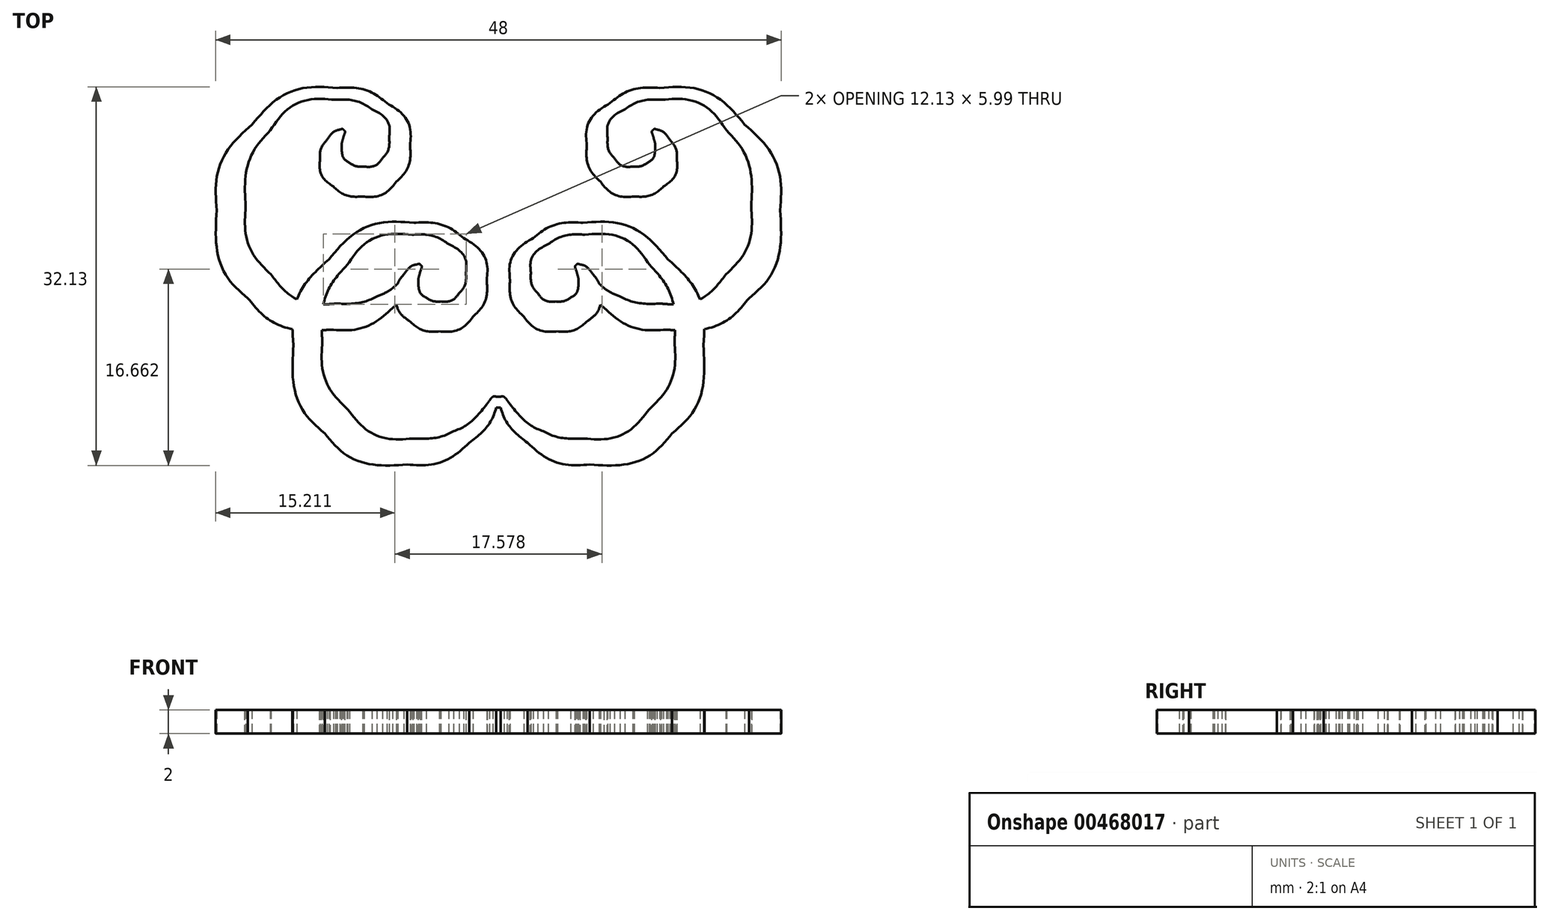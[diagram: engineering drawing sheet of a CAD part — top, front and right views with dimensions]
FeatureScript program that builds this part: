
annotation { "Feature Type Name" : "Feature", "Feature Type Description" : "" }
export const myFeature = defineFeature(function(context is Context, id is Id, definition is map)
    precondition{}
    {
        {
            var Q0;
            Q0=qCreatedBy(makeId("Top.planeOp"),FACE);
            var sketch = newSketch(context, id + "F0", { "sketchPlane" : qUnion([Q0])});
            skFitSpline(sketch, "E0", {"points": [v(-6.53, 0.98) * mm, v(-6.53, 0.79) * mm, v(-6.59, 0.56) * mm, v(-6.7, 0.3) * mm]});
            skFitSpline(sketch, "E1", {"points": [v(-6.7, 0.3) * mm, v(-7.12, -0.8) * mm, v(-7.89, -1.79) * mm, v(-8.99, -2.69) * mm]});
            skFitSpline(sketch, "E2", {"points": [v(-8.99, -2.69) * mm, v(-10.5, -3.92) * mm, v(-12.26, -4.54) * mm, v(-14.26, -4.54) * mm]});
            skFitSpline(sketch, "E3", {"points": [v(-14.26, -4.54) * mm, v(-17.2, -4.54) * mm, v(-19.53, -3.65) * mm, v(-21.26, -1.88) * mm]});
            skFitSpline(sketch, "E4", {"points": [v(-21.26, -1.88) * mm, v(-23.03, -0.07) * mm, v(-23.91, 2.42) * mm, v(-23.91, 5.6) * mm]});
            skFitSpline(sketch, "E5", {"points": [v(-23.91, 5.6) * mm, v(-23.91, 8.38) * mm, v(-22.91, 10.8) * mm, v(-20.9, 12.87) * mm]});
            skFitSpline(sketch, "E6", {"points": [v(-20.9, 12.87) * mm, v(-18.9, 14.94) * mm, v(-16.5, 15.98) * mm, v(-13.7, 15.98) * mm]});
            skFitSpline(sketch, "E7", {"points": [v(-13.7, 15.98) * mm, v(-12.09, 15.98) * mm, v(-10.68, 15.55) * mm, v(-9.47, 14.7) * mm]});
            skFitSpline(sketch, "E8", {"points": [v(-9.47, 14.7) * mm, v(-8.16, 13.75) * mm, v(-7.5, 12.56) * mm, v(-7.5, 11.11) * mm]});
            skFitSpline(sketch, "E9", {"points": [v(-7.5, 11.11) * mm, v(-7.5, 9.9) * mm, v(-7.89, 8.86) * mm, v(-8.66, 8.03) * mm]});
            skFitSpline(sketch, "E10", {"points": [v(-8.66, 8.03) * mm, v(-9.43, 7.19) * mm, v(-10.38, 6.77) * mm, v(-11.52, 6.77) * mm]});
            skFitSpline(sketch, "E11", {"points": [v(-11.52, 6.77) * mm, v(-12.49, 6.77) * mm, v(-13.32, 7.05) * mm, v(-14.02, 7.61) * mm]});
            skFitSpline(sketch, "E12", {"points": [v(-14.02, 7.61) * mm, v(-14.77, 8.22) * mm, v(-15.14, 8.98) * mm, v(-15.14, 9.9) * mm]});
            skFitSpline(sketch, "E13", {"points": [v(-15.14, 9.9) * mm, v(-15.14, 10.5) * mm, v(-14.94, 11.07) * mm, v(-14.54, 11.6) * mm]});
            skFitSpline(sketch, "E14", {"points": [v(-14.54, 11.6) * mm, v(-14.2, 12.06) * mm, v(-13.83, 12.35) * mm, v(-13.45, 12.44) * mm]});
            skFitSpline(sketch, "E15", {"points": [v(-13.45, 12.44) * mm, v(-13.3, 12.5) * mm, v(-13.2, 12.48) * mm, v(-13.11, 12.4) * mm]});
            skFitSpline(sketch, "E16", {"points": [v(-13.11, 12.4) * mm, v(-13.03, 12.32) * mm, v(-13.01, 12.23) * mm, v(-13.05, 12.12) * mm]});
            skFitSpline(sketch, "E17", {"points": [v(-13.05, 12.12) * mm, v(-13.12, 11.93) * mm, v(-13.17, 11.78) * mm, v(-13.2, 11.66) * mm]});
            skFitSpline(sketch, "E18", {"points": [v(-13.2, 11.66) * mm, v(-13.27, 11.39) * mm, v(-13.31, 11.15) * mm, v(-13.31, 10.93) * mm]});
            skFitSpline(sketch, "E19", {"points": [v(-13.31, 10.93) * mm, v(-13.31, 10.78) * mm, v(-13.3, 10.67) * mm, v(-13.3, 10.59) * mm]});
            skFitSpline(sketch, "E20", {"points": [v(-13.3, 10.59) * mm, v(-13.21, 10.17) * mm, v(-13, 9.86) * mm, v(-12.64, 9.63) * mm]});
            skFitSpline(sketch, "E21", {"points": [v(-12.64, 9.63) * mm, v(-12.28, 9.41) * mm, v(-11.87, 9.3) * mm, v(-11.4, 9.3) * mm]});
            skFitSpline(sketch, "E22", {"points": [v(-11.4, 9.3) * mm, v(-10.76, 9.3) * mm, v(-10.24, 9.54) * mm, v(-9.85, 10) * mm]});
            skFitSpline(sketch, "E23", {"points": [v(-9.85, 10) * mm, v(-9.46, 10.48) * mm, v(-9.27, 11.06) * mm, v(-9.27, 11.76) * mm]});
            skFitSpline(sketch, "E24", {"points": [v(-9.27, 11.76) * mm, v(-9.27, 12.78) * mm, v(-9.76, 13.58) * mm, v(-10.74, 14.17) * mm]});
            skFitSpline(sketch, "E25", {"points": [v(-10.74, 14.17) * mm, v(-11.62, 14.7) * mm, v(-12.66, 14.97) * mm, v(-13.86, 14.97) * mm]});
            skFitSpline(sketch, "E26", {"points": [v(-13.86, 14.97) * mm, v(-16.12, 14.97) * mm, v(-17.96, 14.11) * mm, v(-19.36, 12.39) * mm]});
            skFitSpline(sketch, "E27", {"points": [v(-19.36, 12.39) * mm, v(-20.76, 10.67) * mm, v(-21.46, 8.51) * mm, v(-21.46, 5.92) * mm]});
            skFitSpline(sketch, "E28", {"points": [v(-21.46, 5.92) * mm, v(-21.46, 3.67) * mm, v(-20.74, 1.75) * mm, v(-19.3, 0.15) * mm]});
            skFitSpline(sketch, "E29", {"points": [v(-19.3, 0.15) * mm, v(-17.82, -1.5) * mm, v(-15.97, -2.32) * mm, v(-13.78, -2.32) * mm]});
            skFitSpline(sketch, "E30", {"points": [v(-13.78, -2.32) * mm, v(-12.4, -2.32) * mm, v(-11.24, -2.12) * mm, v(-10.33, -1.7) * mm]});
            skFitSpline(sketch, "E31", {"points": [v(-10.33, -1.7) * mm, v(-9.4, -1.3) * mm, v(-8.47, -0.54) * mm, v(-7.5, 0.57) * mm]});
            skFitSpline(sketch, "E32", {"points": [v(-7.5, 0.57) * mm, v(-7.49, 0.6) * mm, v(-7.4, 0.71) * mm, v(-7.26, 0.92) * mm]});
            skFitSpline(sketch, "E33", {"points": [v(-7.26, 0.92) * mm, v(-7.15, 1.06) * mm, v(-7.06, 1.16) * mm, v(-6.98, 1.22) * mm]});
            skFitSpline(sketch, "E34", {"points": [v(-6.98, 1.22) * mm, v(-6.91, 1.26) * mm, v(-6.82, 1.26) * mm, v(-6.7, 1.23) * mm]});
            skFitSpline(sketch, "E35", {"points": [v(-6.7, 1.23) * mm, v(-6.6, 1.2) * mm, v(-6.53, 1.1) * mm, v(-6.53, 0.98) * mm]});
            skFitSpline(sketch, "E36", {"points": [v(-0.02, -10.47) * mm, v(-0.02, -10.66) * mm, v(-0.08, -10.89) * mm, v(-0.18, -11.15) * mm]});
            skFitSpline(sketch, "E37", {"points": [v(-0.18, -11.15) * mm, v(-0.61, -12.24) * mm, v(-1.38, -13.23) * mm, v(-2.48, -14.13) * mm]});
            skFitSpline(sketch, "E38", {"points": [v(-2.48, -14.13) * mm, v(-4, -15.36) * mm, v(-5.75, -15.98) * mm, v(-7.75, -15.98) * mm]});
            skFitSpline(sketch, "E39", {"points": [v(-7.75, -15.98) * mm, v(-10.68, -15.98) * mm, v(-13.02, -15.1) * mm, v(-14.75, -13.33) * mm]});
            skFitSpline(sketch, "E40", {"points": [v(-14.75, -13.33) * mm, v(-16.52, -11.52) * mm, v(-17.4, -9.02) * mm, v(-17.4, -5.84) * mm]});
            skFitSpline(sketch, "E41", {"points": [v(-17.4, -5.84) * mm, v(-17.4, -3.07) * mm, v(-16.4, -0.64) * mm, v(-14.4, 1.43) * mm]});
            skFitSpline(sketch, "E42", {"points": [v(-14.4, 1.43) * mm, v(-12.39, 3.5) * mm, v(-9.99, 4.54) * mm, v(-7.18, 4.54) * mm]});
            skFitSpline(sketch, "E43", {"points": [v(-7.18, 4.54) * mm, v(-5.57, 4.54) * mm, v(-4.17, 4.1) * mm, v(-2.96, 3.25) * mm]});
            skFitSpline(sketch, "E44", {"points": [v(-2.96, 3.25) * mm, v(-1.64, 2.3) * mm, v(-0.99, 1.12) * mm, v(-0.99, -0.33) * mm]});
            skFitSpline(sketch, "E45", {"points": [v(-0.99, -0.33) * mm, v(-0.99, -1.55) * mm, v(-1.37, -2.58) * mm, v(-2.14, -3.42) * mm]});
            skFitSpline(sketch, "E46", {"points": [v(-2.14, -3.42) * mm, v(-2.92, -4.26) * mm, v(-3.87, -4.68) * mm, v(-5.01, -4.68) * mm]});
            skFitSpline(sketch, "E47", {"points": [v(-5.01, -4.68) * mm, v(-5.98, -4.68) * mm, v(-6.8, -4.4) * mm, v(-7.5, -3.83) * mm]});
            skFitSpline(sketch, "E48", {"points": [v(-7.5, -3.83) * mm, v(-8.26, -3.23) * mm, v(-8.63, -2.46) * mm, v(-8.63, -1.54) * mm]});
            skFitSpline(sketch, "E49", {"points": [v(-8.63, -1.54) * mm, v(-8.63, -0.94) * mm, v(-8.43, -0.37) * mm, v(-8.03, 0.15) * mm]});
            skFitSpline(sketch, "E50", {"points": [v(-8.03, 0.15) * mm, v(-7.68, 0.62) * mm, v(-7.32, 0.9) * mm, v(-6.94, 1) * mm]});
            skFitSpline(sketch, "E51", {"points": [v(-6.94, 1) * mm, v(-6.8, 1.05) * mm, v(-6.68, 1.04) * mm, v(-6.6, 0.95) * mm]});
            skFitSpline(sketch, "E52", {"points": [v(-6.6, 0.95) * mm, v(-6.52, 0.87) * mm, v(-6.5, 0.78) * mm, v(-6.54, 0.67) * mm]});
            skFitSpline(sketch, "E53", {"points": [v(-6.54, 0.67) * mm, v(-6.6, 0.49) * mm, v(-6.65, 0.33) * mm, v(-6.68, 0.21) * mm]});
            skFitSpline(sketch, "E54", {"points": [v(-6.68, 0.21) * mm, v(-6.76, -0.06) * mm, v(-6.8, -0.3) * mm, v(-6.8, -0.51) * mm]});
            skFitSpline(sketch, "E55", {"points": [v(-6.8, -0.51) * mm, v(-6.8, -0.66) * mm, v(-6.8, -0.77) * mm, v(-6.78, -0.86) * mm]});
            skFitSpline(sketch, "E56", {"points": [v(-6.78, -0.86) * mm, v(-6.7, -1.27) * mm, v(-6.48, -1.59) * mm, v(-6.13, -1.81) * mm]});
            skFitSpline(sketch, "E57", {"points": [v(-6.13, -1.81) * mm, v(-5.77, -2.03) * mm, v(-5.36, -2.14) * mm, v(-4.89, -2.14) * mm]});
            skFitSpline(sketch, "E58", {"points": [v(-4.89, -2.14) * mm, v(-4.25, -2.14) * mm, v(-3.73, -1.9) * mm, v(-3.34, -1.44) * mm]});
            skFitSpline(sketch, "E59", {"points": [v(-3.34, -1.44) * mm, v(-2.95, -0.97) * mm, v(-2.76, -0.39) * mm, v(-2.76, 0.31) * mm]});
            skFitSpline(sketch, "E60", {"points": [v(-2.76, 0.31) * mm, v(-2.76, 1.33) * mm, v(-3.25, 2.13) * mm, v(-4.23, 2.72) * mm]});
            skFitSpline(sketch, "E61", {"points": [v(-4.23, 2.72) * mm, v(-5.11, 3.26) * mm, v(-6.15, 3.53) * mm, v(-7.34, 3.53) * mm]});
            skFitSpline(sketch, "E62", {"points": [v(-7.34, 3.53) * mm, v(-9.6, 3.53) * mm, v(-11.44, 2.67) * mm, v(-12.84, 0.94) * mm]});
            skFitSpline(sketch, "E63", {"points": [v(-12.84, 0.94) * mm, v(-14.25, -0.78) * mm, v(-14.95, -2.93) * mm, v(-14.95, -5.52) * mm]});
            skFitSpline(sketch, "E64", {"points": [v(-14.95, -5.52) * mm, v(-14.95, -7.77) * mm, v(-14.23, -9.7) * mm, v(-12.8, -11.3) * mm]});
            skFitSpline(sketch, "E65", {"points": [v(-12.8, -11.3) * mm, v(-11.3, -12.94) * mm, v(-9.46, -13.77) * mm, v(-7.26, -13.77) * mm]});
            skFitSpline(sketch, "E66", {"points": [v(-7.26, -13.77) * mm, v(-5.88, -13.77) * mm, v(-4.73, -13.56) * mm, v(-3.81, -13.15) * mm]});
            skFitSpline(sketch, "E67", {"points": [v(-3.81, -13.15) * mm, v(-2.9, -12.75) * mm, v(-1.95, -11.98) * mm, v(-0.99, -10.87) * mm]});
            skFitSpline(sketch, "E68", {"points": [v(-0.99, -10.87) * mm, v(-0.97, -10.85) * mm, v(-0.9, -10.73) * mm, v(-0.75, -10.53) * mm]});
            skFitSpline(sketch, "E69", {"points": [v(-0.75, -10.53) * mm, v(-0.64, -10.38) * mm, v(-0.55, -10.28) * mm, v(-0.46, -10.23) * mm]});
            skFitSpline(sketch, "E70", {"points": [v(-0.46, -10.23) * mm, v(-0.4, -10.19) * mm, v(-0.3, -10.18) * mm, v(-0.2, -10.22) * mm]});
            skFitSpline(sketch, "E71", {"points": [v(-0.2, -10.22) * mm, v(-0.08, -10.25) * mm, v(-0.02, -10.34) * mm, v(-0.02, -10.47) * mm]});
            skFitSpline(sketch, "E72", {"points": [v(6.7, 1.23) * mm, v(6.82, 1.26) * mm, v(6.91, 1.26) * mm, v(6.98, 1.22) * mm]});
            skFitSpline(sketch, "E73", {"points": [v(6.98, 1.22) * mm, v(7.06, 1.16) * mm, v(7.15, 1.06) * mm, v(7.26, 0.92) * mm]});
            skFitSpline(sketch, "E74", {"points": [v(7.26, 0.92) * mm, v(7.4, 0.71) * mm, v(7.49, 0.6) * mm, v(7.5, 0.57) * mm]});
            skFitSpline(sketch, "E75", {"points": [v(7.5, 0.57) * mm, v(8.47, -0.54) * mm, v(9.4, -1.3) * mm, v(10.33, -1.7) * mm]});
            skFitSpline(sketch, "E76", {"points": [v(10.33, -1.7) * mm, v(11.24, -2.12) * mm, v(12.4, -2.32) * mm, v(13.78, -2.32) * mm]});
            skFitSpline(sketch, "E77", {"points": [v(13.78, -2.32) * mm, v(15.97, -2.32) * mm, v(17.82, -1.5) * mm, v(19.3, 0.15) * mm]});
            skFitSpline(sketch, "E78", {"points": [v(19.3, 0.15) * mm, v(20.74, 1.75) * mm, v(21.46, 3.67) * mm, v(21.46, 5.92) * mm]});
            skFitSpline(sketch, "E79", {"points": [v(21.46, 5.92) * mm, v(21.46, 8.51) * mm, v(20.76, 10.67) * mm, v(19.36, 12.39) * mm]});
            skFitSpline(sketch, "E80", {"points": [v(19.36, 12.39) * mm, v(17.96, 14.11) * mm, v(16.12, 14.97) * mm, v(13.86, 14.97) * mm]});
            skFitSpline(sketch, "E81", {"points": [v(13.86, 14.97) * mm, v(12.66, 14.97) * mm, v(11.62, 14.7) * mm, v(10.74, 14.17) * mm]});
            skFitSpline(sketch, "E82", {"points": [v(10.74, 14.17) * mm, v(9.76, 13.58) * mm, v(9.27, 12.78) * mm, v(9.27, 11.76) * mm]});
            skFitSpline(sketch, "E83", {"points": [v(9.27, 11.76) * mm, v(9.27, 11.06) * mm, v(9.46, 10.48) * mm, v(9.85, 10) * mm]});
            skFitSpline(sketch, "E84", {"points": [v(9.85, 10) * mm, v(10.24, 9.54) * mm, v(10.76, 9.3) * mm, v(11.4, 9.3) * mm]});
            skFitSpline(sketch, "E85", {"points": [v(11.4, 9.3) * mm, v(11.87, 9.3) * mm, v(12.28, 9.41) * mm, v(12.64, 9.63) * mm]});
            skFitSpline(sketch, "E86", {"points": [v(12.64, 9.63) * mm, v(13, 9.86) * mm, v(13.21, 10.17) * mm, v(13.3, 10.59) * mm]});
            skFitSpline(sketch, "E87", {"points": [v(13.3, 10.59) * mm, v(13.3, 10.67) * mm, v(13.31, 10.78) * mm, v(13.31, 10.93) * mm]});
            skFitSpline(sketch, "E88", {"points": [v(13.31, 10.93) * mm, v(13.31, 11.15) * mm, v(13.27, 11.39) * mm, v(13.2, 11.66) * mm]});
            skFitSpline(sketch, "E89", {"points": [v(13.2, 11.66) * mm, v(13.17, 11.78) * mm, v(13.12, 11.93) * mm, v(13.05, 12.12) * mm]});
            skFitSpline(sketch, "E90", {"points": [v(13.05, 12.12) * mm, v(13.01, 12.23) * mm, v(13.03, 12.32) * mm, v(13.11, 12.4) * mm]});
            skFitSpline(sketch, "E91", {"points": [v(13.11, 12.4) * mm, v(13.2, 12.48) * mm, v(13.3, 12.5) * mm, v(13.45, 12.44) * mm]});
            skFitSpline(sketch, "E92", {"points": [v(13.45, 12.44) * mm, v(13.83, 12.35) * mm, v(14.2, 12.06) * mm, v(14.54, 11.6) * mm]});
            skFitSpline(sketch, "E93", {"points": [v(14.54, 11.6) * mm, v(14.94, 11.07) * mm, v(15.14, 10.5) * mm, v(15.14, 9.9) * mm]});
            skFitSpline(sketch, "E94", {"points": [v(15.14, 9.9) * mm, v(15.14, 8.98) * mm, v(14.77, 8.22) * mm, v(14.02, 7.61) * mm]});
            skFitSpline(sketch, "E95", {"points": [v(14.02, 7.61) * mm, v(13.32, 7.05) * mm, v(12.49, 6.77) * mm, v(11.52, 6.77) * mm]});
            skFitSpline(sketch, "E96", {"points": [v(11.52, 6.77) * mm, v(10.38, 6.77) * mm, v(9.43, 7.19) * mm, v(8.66, 8.03) * mm]});
            skFitSpline(sketch, "E97", {"points": [v(8.66, 8.03) * mm, v(7.89, 8.86) * mm, v(7.5, 9.9) * mm, v(7.5, 11.11) * mm]});
            skFitSpline(sketch, "E98", {"points": [v(7.5, 11.11) * mm, v(7.5, 12.56) * mm, v(8.16, 13.75) * mm, v(9.47, 14.7) * mm]});
            skFitSpline(sketch, "E99", {"points": [v(9.47, 14.7) * mm, v(10.68, 15.55) * mm, v(12.09, 15.98) * mm, v(13.7, 15.98) * mm]});
            skFitSpline(sketch, "E100", {"points": [v(13.7, 15.98) * mm, v(16.5, 15.98) * mm, v(18.9, 14.94) * mm, v(20.9, 12.87) * mm]});
            skFitSpline(sketch, "E101", {"points": [v(20.9, 12.87) * mm, v(22.91, 10.8) * mm, v(23.91, 8.38) * mm, v(23.91, 5.6) * mm]});
            skFitSpline(sketch, "E102", {"points": [v(23.91, 5.6) * mm, v(23.91, 2.42) * mm, v(23.03, -0.07) * mm, v(21.26, -1.88) * mm]});
            skFitSpline(sketch, "E103", {"points": [v(21.26, -1.88) * mm, v(19.53, -3.65) * mm, v(17.2, -4.54) * mm, v(14.26, -4.54) * mm]});
            skFitSpline(sketch, "E104", {"points": [v(14.26, -4.54) * mm, v(12.26, -4.54) * mm, v(10.5, -3.92) * mm, v(8.99, -2.68) * mm]});
            skFitSpline(sketch, "E105", {"points": [v(8.99, -2.68) * mm, v(7.89, -1.79) * mm, v(7.12, -0.8) * mm, v(6.7, 0.3) * mm]});
            skFitSpline(sketch, "E106", {"points": [v(6.7, 0.3) * mm, v(6.59, 0.56) * mm, v(6.53, 0.79) * mm, v(6.53, 0.98) * mm]});
            skFitSpline(sketch, "E107", {"points": [v(6.53, 0.98) * mm, v(6.53, 1.1) * mm, v(6.6, 1.2) * mm, v(6.7, 1.23) * mm]});
            skFitSpline(sketch, "E108", {"points": [v(0.2, -10.22) * mm, v(0.3, -10.18) * mm, v(0.4, -10.19) * mm, v(0.46, -10.23) * mm]});
            skFitSpline(sketch, "E109", {"points": [v(0.46, -10.23) * mm, v(0.55, -10.28) * mm, v(0.64, -10.38) * mm, v(0.75, -10.53) * mm]});
            skFitSpline(sketch, "E110", {"points": [v(0.75, -10.53) * mm, v(0.9, -10.73) * mm, v(0.97, -10.85) * mm, v(0.99, -10.87) * mm]});
            skFitSpline(sketch, "E111", {"points": [v(0.99, -10.87) * mm, v(1.95, -11.98) * mm, v(2.9, -12.75) * mm, v(3.81, -13.15) * mm]});
            skFitSpline(sketch, "E112", {"points": [v(3.81, -13.15) * mm, v(4.73, -13.56) * mm, v(5.88, -13.77) * mm, v(7.26, -13.77) * mm]});
            skFitSpline(sketch, "E113", {"points": [v(7.26, -13.77) * mm, v(9.46, -13.77) * mm, v(11.3, -12.94) * mm, v(12.8, -11.3) * mm]});
            skFitSpline(sketch, "E114", {"points": [v(12.8, -11.3) * mm, v(14.23, -9.7) * mm, v(14.95, -7.77) * mm, v(14.95, -5.52) * mm]});
            skFitSpline(sketch, "E115", {"points": [v(14.95, -5.52) * mm, v(14.95, -2.93) * mm, v(14.25, -0.78) * mm, v(12.84, 0.94) * mm]});
            skFitSpline(sketch, "E116", {"points": [v(12.84, 0.94) * mm, v(11.44, 2.67) * mm, v(9.6, 3.53) * mm, v(7.34, 3.53) * mm]});
            skFitSpline(sketch, "E117", {"points": [v(7.34, 3.53) * mm, v(6.15, 3.53) * mm, v(5.11, 3.26) * mm, v(4.23, 2.72) * mm]});
            skFitSpline(sketch, "E118", {"points": [v(4.23, 2.72) * mm, v(3.25, 2.13) * mm, v(2.76, 1.33) * mm, v(2.76, 0.31) * mm]});
            skFitSpline(sketch, "E119", {"points": [v(2.76, 0.31) * mm, v(2.76, -0.39) * mm, v(2.95, -0.97) * mm, v(3.34, -1.44) * mm]});
            skFitSpline(sketch, "E120", {"points": [v(3.34, -1.44) * mm, v(3.73, -1.9) * mm, v(4.25, -2.14) * mm, v(4.89, -2.14) * mm]});
            skFitSpline(sketch, "E121", {"points": [v(4.89, -2.14) * mm, v(5.36, -2.14) * mm, v(5.77, -2.03) * mm, v(6.13, -1.81) * mm]});
            skFitSpline(sketch, "E122", {"points": [v(6.13, -1.81) * mm, v(6.48, -1.59) * mm, v(6.7, -1.27) * mm, v(6.78, -0.86) * mm]});
            skFitSpline(sketch, "E123", {"points": [v(6.78, -0.86) * mm, v(6.8, -0.77) * mm, v(6.8, -0.66) * mm, v(6.8, -0.51) * mm]});
            skFitSpline(sketch, "E124", {"points": [v(6.8, -0.51) * mm, v(6.8, -0.3) * mm, v(6.76, -0.06) * mm, v(6.68, 0.21) * mm]});
            skFitSpline(sketch, "E125", {"points": [v(6.68, 0.21) * mm, v(6.65, 0.33) * mm, v(6.6, 0.49) * mm, v(6.54, 0.67) * mm]});
            skFitSpline(sketch, "E126", {"points": [v(6.54, 0.67) * mm, v(6.5, 0.78) * mm, v(6.52, 0.87) * mm, v(6.6, 0.95) * mm]});
            skFitSpline(sketch, "E127", {"points": [v(6.6, 0.95) * mm, v(6.68, 1.04) * mm, v(6.8, 1.05) * mm, v(6.94, 1) * mm]});
            skFitSpline(sketch, "E128", {"points": [v(6.94, 1) * mm, v(7.32, 0.9) * mm, v(7.68, 0.62) * mm, v(8.03, 0.15) * mm]});
            skFitSpline(sketch, "E129", {"points": [v(8.03, 0.15) * mm, v(8.43, -0.37) * mm, v(8.63, -0.94) * mm, v(8.63, -1.54) * mm]});
            skFitSpline(sketch, "E130", {"points": [v(8.63, -1.54) * mm, v(8.63, -2.46) * mm, v(8.26, -3.23) * mm, v(7.5, -3.83) * mm]});
            skFitSpline(sketch, "E131", {"points": [v(7.5, -3.83) * mm, v(6.8, -4.4) * mm, v(5.98, -4.68) * mm, v(5.01, -4.68) * mm]});
            skFitSpline(sketch, "E132", {"points": [v(5.01, -4.68) * mm, v(3.87, -4.68) * mm, v(2.92, -4.26) * mm, v(2.14, -3.42) * mm]});
            skFitSpline(sketch, "E133", {"points": [v(2.14, -3.42) * mm, v(1.37, -2.58) * mm, v(0.99, -1.55) * mm, v(0.99, -0.33) * mm]});
            skFitSpline(sketch, "E134", {"points": [v(0.99, -0.33) * mm, v(0.99, 1.12) * mm, v(1.64, 2.3) * mm, v(2.96, 3.25) * mm]});
            skFitSpline(sketch, "E135", {"points": [v(2.96, 3.25) * mm, v(4.17, 4.1) * mm, v(5.57, 4.54) * mm, v(7.18, 4.54) * mm]});
            skFitSpline(sketch, "E136", {"points": [v(7.18, 4.54) * mm, v(9.99, 4.54) * mm, v(12.39, 3.5) * mm, v(14.4, 1.43) * mm]});
            skFitSpline(sketch, "E137", {"points": [v(14.4, 1.43) * mm, v(16.4, -0.64) * mm, v(17.4, -3.07) * mm, v(17.4, -5.84) * mm]});
            skFitSpline(sketch, "E138", {"points": [v(17.4, -5.84) * mm, v(17.4, -9.02) * mm, v(16.52, -11.52) * mm, v(14.75, -13.33) * mm]});
            skFitSpline(sketch, "E139", {"points": [v(14.75, -13.33) * mm, v(13.02, -15.1) * mm, v(10.68, -15.98) * mm, v(7.75, -15.98) * mm]});
            skFitSpline(sketch, "E140", {"points": [v(7.75, -15.98) * mm, v(5.75, -15.98) * mm, v(4, -15.36) * mm, v(2.48, -14.13) * mm]});
            skFitSpline(sketch, "E141", {"points": [v(2.48, -14.13) * mm, v(1.38, -13.23) * mm, v(0.61, -12.24) * mm, v(0.18, -11.15) * mm]});
            skFitSpline(sketch, "E142", {"points": [v(0.18, -11.15) * mm, v(0.08, -10.89) * mm, v(0.02, -10.66) * mm, v(0.02, -10.47) * mm]});
            skFitSpline(sketch, "E143", {"points": [v(0.02, -10.47) * mm, v(0.02, -10.34) * mm, v(0.08, -10.25) * mm, v(0.2, -10.22) * mm]});
            skLineSegment(sketch, "E144", {"start": v(-0.2, -10.22) * mm, "end": v(0.2, -10.22) * mm});
            skLineSegment(sketch, "E145", {"start": v(-0.18, -11.15) * mm, "end": v(0.18, -11.15) * mm});
            skSolve(sketch);
        }
        {
            var Q0;
            {var subQ0=sQuery(id+"F0.wireOp",EDGE,"E4");Q0=makeQuery(id+"F0.imprint","IMPRINT",FACE,{"disambiguationData":[TD([[makeQuery(id+"F0.imprint","IMPRINT",EDGE,{"derivedFrom":subQ0}),-1.0]])]});}
            var Q1;
            {var subQ0=sQuery(id+"F0.wireOp",EDGE,"E63");var subQ1=sQuery(id+"F0.wireOp",EDGE,"E3");var subQ2=makeQuery(id+"F0.imprint","INTERSECT",VERTEX,{"derivedFrom":[subQ1,subQ0]});Q1=makeQuery(id+"F0.imprint","IMPRINT",FACE,{"disambiguationData":[TD([[makeQuery(id+"F0.imprint","IMPRINT",EDGE,{"disambiguationData":[TD([[subQ2,-1.0]])],"derivedFrom":subQ1}),-1.0]])]});}
            var Q2;
            {var subQ14=sQuery(id+"F0.wireOp",EDGE,"E42");Q2=makeQuery(id+"F0.imprint","IMPRINT",FACE,{"disambiguationData":[TD([[makeQuery(id+"F0.imprint","IMPRINT",EDGE,{"derivedFrom":subQ14}),-1.0]])]});}
            var Q3;
            Q3=makeQuery(id+"F0.imprint","IMPRINT",FACE,{"disambiguationData":[TD([[makeQuery(id+"F0.imprint","IMPRINT",EDGE,{"derivedFrom":sQuery(id+"F0.wireOp",EDGE,"E36")}),-1.0]])]});
            var Q4;
            {var subQ5=sQuery(id+"F0.wireOp",EDGE,"E2");Q4=makeQuery(id+"F0.imprint","IMPRINT",FACE,{"disambiguationData":[TD([[makeQuery(id+"F0.imprint","IMPRINT",EDGE,{"derivedFrom":subQ5}),-1.0]])]});}
            var Q5;
            {var subQ15=sQuery(id+"F0.wireOp",EDGE,"E51");Q5=makeQuery(id+"F0.imprint","IMPRINT",FACE,{"disambiguationData":[TD([[makeQuery(id+"F0.imprint","IMPRINT",EDGE,{"derivedFrom":subQ15}),-1.0]])]});}
            var Q6;
            {var subQ0=sQuery(id+"F0.wireOp",EDGE,"E32");var subQ1=sQuery(id+"F0.wireOp",EDGE,"E31");var subQ2=makeQuery(id+"F0.imprint","INTERSECT",VERTEX,{"derivedFrom":[subQ1,subQ0]});Q6=makeQuery(id+"F0.imprint","IMPRINT",FACE,{"disambiguationData":[TD([[makeQuery(id+"F0.imprint","IMPRINT",EDGE,{"disambiguationData":[TD([[subQ2,1.0]])],"derivedFrom":subQ1}),1.0]])]});}
            var Q7;
            Q7=makeQuery(id+"F0.imprint","IMPRINT",FACE,{"disambiguationData":[TD([[makeQuery(id+"F0.imprint","IMPRINT",EDGE,{"derivedFrom":sQuery(id+"F0.wireOp",EDGE,"E108")}),-1.0]])]});
            var Q8;
            {var subQ0=sQuery(id+"F0.wireOp",EDGE,"E137");var subQ1=sQuery(id+"F0.wireOp",EDGE,"E77");var subQ2=makeQuery(id+"F0.imprint","INTERSECT",VERTEX,{"derivedFrom":[subQ1,subQ0]});Q8=makeQuery(id+"F0.imprint","IMPRINT",FACE,{"disambiguationData":[TD([[makeQuery(id+"F0.imprint","IMPRINT",EDGE,{"disambiguationData":[TD([[subQ2,1.0]])],"derivedFrom":subQ1}),-1.0]])]});}
            var Q9;
            {var subQ9=sQuery(id+"F0.wireOp",EDGE,"E116");Q9=makeQuery(id+"F0.imprint","IMPRINT",FACE,{"disambiguationData":[TD([[makeQuery(id+"F0.imprint","IMPRINT",EDGE,{"derivedFrom":subQ9}),-1.0]])]});}
            var Q10;
            {var subQ10=sQuery(id+"F0.wireOp",EDGE,"E76");Q10=makeQuery(id+"F0.imprint","IMPRINT",FACE,{"disambiguationData":[TD([[makeQuery(id+"F0.imprint","IMPRINT",EDGE,{"derivedFrom":subQ10}),-1.0]])]});}
            var Q11;
            {var subQ15=sQuery(id+"F0.wireOp",EDGE,"E127");Q11=makeQuery(id+"F0.imprint","IMPRINT",FACE,{"disambiguationData":[TD([[makeQuery(id+"F0.imprint","IMPRINT",EDGE,{"derivedFrom":subQ15}),-1.0]])]});}
            var Q12;
            {var subQ0=sQuery(id+"F0.wireOp",EDGE,"E75");var subQ1=sQuery(id+"F0.wireOp",EDGE,"E74");var subQ2=makeQuery(id+"F0.imprint","INTERSECT",VERTEX,{"derivedFrom":[subQ1,subQ0]});Q12=makeQuery(id+"F0.imprint","IMPRINT",FACE,{"disambiguationData":[TD([[makeQuery(id+"F0.imprint","IMPRINT",EDGE,{"disambiguationData":[TD([[subQ2,1.0]])],"derivedFrom":subQ1}),1.0]])]});}
            var Q13;
            {var subQ0=sQuery(id+"F0.wireOp",EDGE,"E78");Q13=makeQuery(id+"F0.imprint","IMPRINT",FACE,{"disambiguationData":[TD([[makeQuery(id+"F0.imprint","IMPRINT",EDGE,{"derivedFrom":subQ0}),-1.0]])]});}
            var Q14;
            Q14=makeQuery(id+"F0.imprint","IMPRINT",FACE,{"disambiguationData":[TD([[makeQuery(id+"F0.imprint","IMPRINT",EDGE,{"derivedFrom":sQuery(id+"F0.wireOp",EDGE,"E36")}),1.0]])]});
            extrude(context, id + "F1", {"entities" : qUnion([Q0, Q1, Q2, Q3, Q4, Q5, Q6, Q7, Q8, Q9, Q10, Q11, Q12, Q13, Q14]), "depth" : 2 * mm, "offsetDistance" : 25 * mm});
        }
    });
